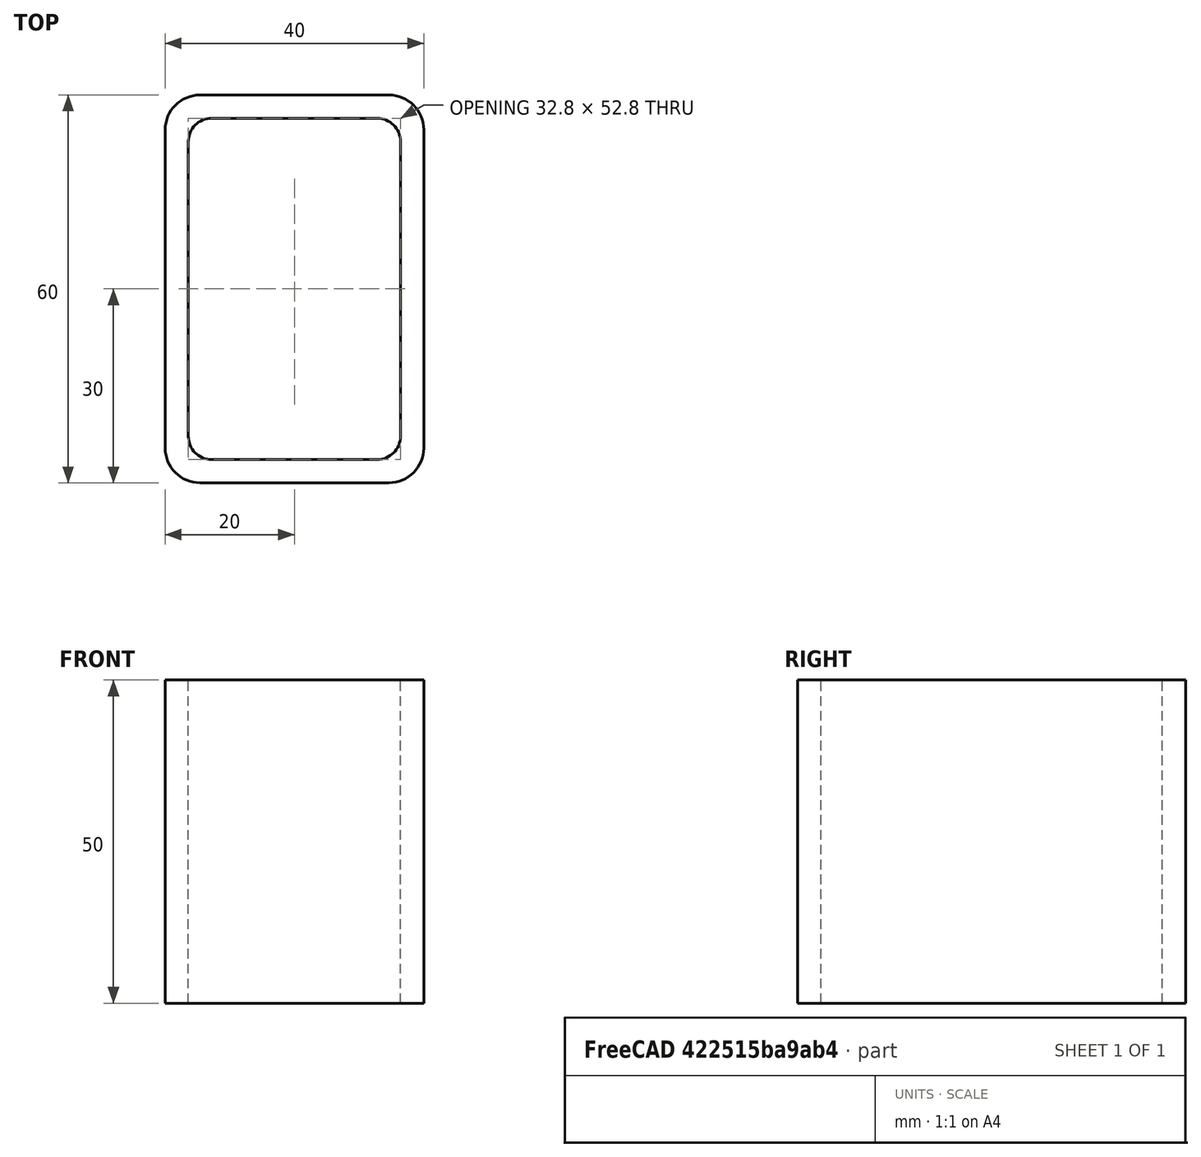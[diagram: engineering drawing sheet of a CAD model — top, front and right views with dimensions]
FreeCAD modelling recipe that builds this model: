
FCSTD DOCUMENT  (FreeCAD 0.15R4671 (Git))
Label: Rectangular hollow section 60x40x3.6 EN10219 S235JRH
License: All rights reserved
LicenseURL: http://en.wikipedia.org/wiki/All_rights_reserved
objects: Sketcher::SketchObject×1, Part::Extrusion×1
note: 2 computed .brp shape members not serialized (recipe doc carries the construction recipe); baked Part::Feature solids carry a one-line shape summary decoded from their .brp

FEATURE [Sketcher::SketchObject] Sketch
  sketch-geometry (16):
    g0: LineSegment StartX=-12.8 StartY=26.4 StartZ=0 EndX=12.8 EndY=26.4 EndZ=0
    g1: LineSegment StartX=16.4 StartY=22.8 StartZ=0 EndX=16.4 EndY=-22.8 EndZ=0
    g2: LineSegment StartX=12.8 StartY=-26.4 StartZ=0 EndX=-12.8 EndY=-26.4 EndZ=0
    g3: LineSegment StartX=-16.4 StartY=-22.8 StartZ=0 EndX=-16.4 EndY=22.8 EndZ=0
    g4: LineSegment StartX=-14.6 StartY=30 StartZ=0 EndX=14.6 EndY=30 EndZ=0
    g5: LineSegment StartX=20 StartY=24.6 StartZ=0 EndX=20 EndY=-24.6 EndZ=0
    g6: LineSegment StartX=14.6 StartY=-30 StartZ=0 EndX=-14.6 EndY=-30 EndZ=0
    g7: LineSegment StartX=-20 StartY=-24.6 StartZ=0 EndX=-20 EndY=24.6 EndZ=0
    g8: ArcOfCircle CenterX=-12.8 CenterY=22.8 CenterZ=0 NormalX=0 NormalY=0 NormalZ=1 Radius=3.6 StartAngle=1.5708 EndAngle=3.14159
    g9: ArcOfCircle CenterX=12.8 CenterY=22.8 CenterZ=0 NormalX=0 NormalY=0 NormalZ=1 Radius=3.6 StartAngle=0 EndAngle=1.5708
    g10: ArcOfCircle CenterX=12.8 CenterY=-22.8 CenterZ=0 NormalX=0 NormalY=0 NormalZ=1 Radius=3.6 StartAngle=4.71239 EndAngle=6.28319
    g11: ArcOfCircle CenterX=-12.8 CenterY=-22.8 CenterZ=0 NormalX=0 NormalY=0 NormalZ=1 Radius=3.6 StartAngle=3.14159 EndAngle=4.71239
    g12: ArcOfCircle CenterX=14.6 CenterY=24.6 CenterZ=0 NormalX=0 NormalY=0 NormalZ=1 Radius=5.4 StartAngle=0 EndAngle=1.5708
    g13: ArcOfCircle CenterX=14.6 CenterY=-24.6 CenterZ=0 NormalX=0 NormalY=0 NormalZ=1 Radius=5.4 StartAngle=4.71239 EndAngle=6.28319
    g14: ArcOfCircle CenterX=-14.6 CenterY=-24.6 CenterZ=0 NormalX=0 NormalY=0 NormalZ=1 Radius=5.4 StartAngle=3.14159 EndAngle=4.71239
    g15: ArcOfCircle CenterX=-14.6 CenterY=24.6 CenterZ=0 NormalX=0 NormalY=0 NormalZ=1 Radius=5.4 StartAngle=1.5708 EndAngle=3.14159
  constraints (36):
    c: Horizontal(g2)
    c: Vertical(g3)
    c: Horizontal(g6)
    c: Vertical(g7)
    c: Tangent(g3,g8) = 1.5708
    c: Tangent(g0,g8) = 1.5708
    c: Tangent(g0,g9) = 1.5708
    c: Tangent(g1,g9) = 1.5708
    c: Tangent(g1,g10) = 1.5708
    c: Tangent(g2,g10) = 1.5708
    c: Tangent(g2,g11) = 1.5708
    c: Tangent(g3,g11) = 1.5708
    c: Tangent(g4,g12) = 1.5708
    c: Tangent(g5,g12) = 1.5708
    c: Tangent(g5,g13) = 1.5708
    c: Tangent(g6,g13) = 1.5708
    c: Tangent(g6,g14) = 1.5708
    c: Tangent(g7,g14) = 1.5708
    c: Tangent(g7,g15) = 1.5708
    c: Tangent(g4,g15) = 1.5708
    c: Equal(g9,g8)
    c: Equal(g9,g11)
    c: Equal(g9,g10)
    c: Equal(g12,g15)
    c: Equal(g12,g14)
    c: Equal(g12,g13)
    c: Symmetric(g4,g6,g-1)
    c: Symmetric(g7,g5,g-2)
    c: DistanceY(g4,g6) = -60
    c: DistanceX(g7,g5) = 40
    c: Symmetric(g3,g1,g-2)
    c: Symmetric(g0,g2,g-1)
    c: DistanceY(g0,g4) = 3.6
    c: DistanceX(g5,g1) = -3.6
    c: Radius(g9) = 3.6
    c: Radius(g12) = 5.4
FEATURE [Part::Extrusion] Extrude  label="Rectangular hollow section 60x40x3.6 EN10219 S235JRH"
  Base = -> Sketch
  Dir = (0,0,50)
  Solid = true
